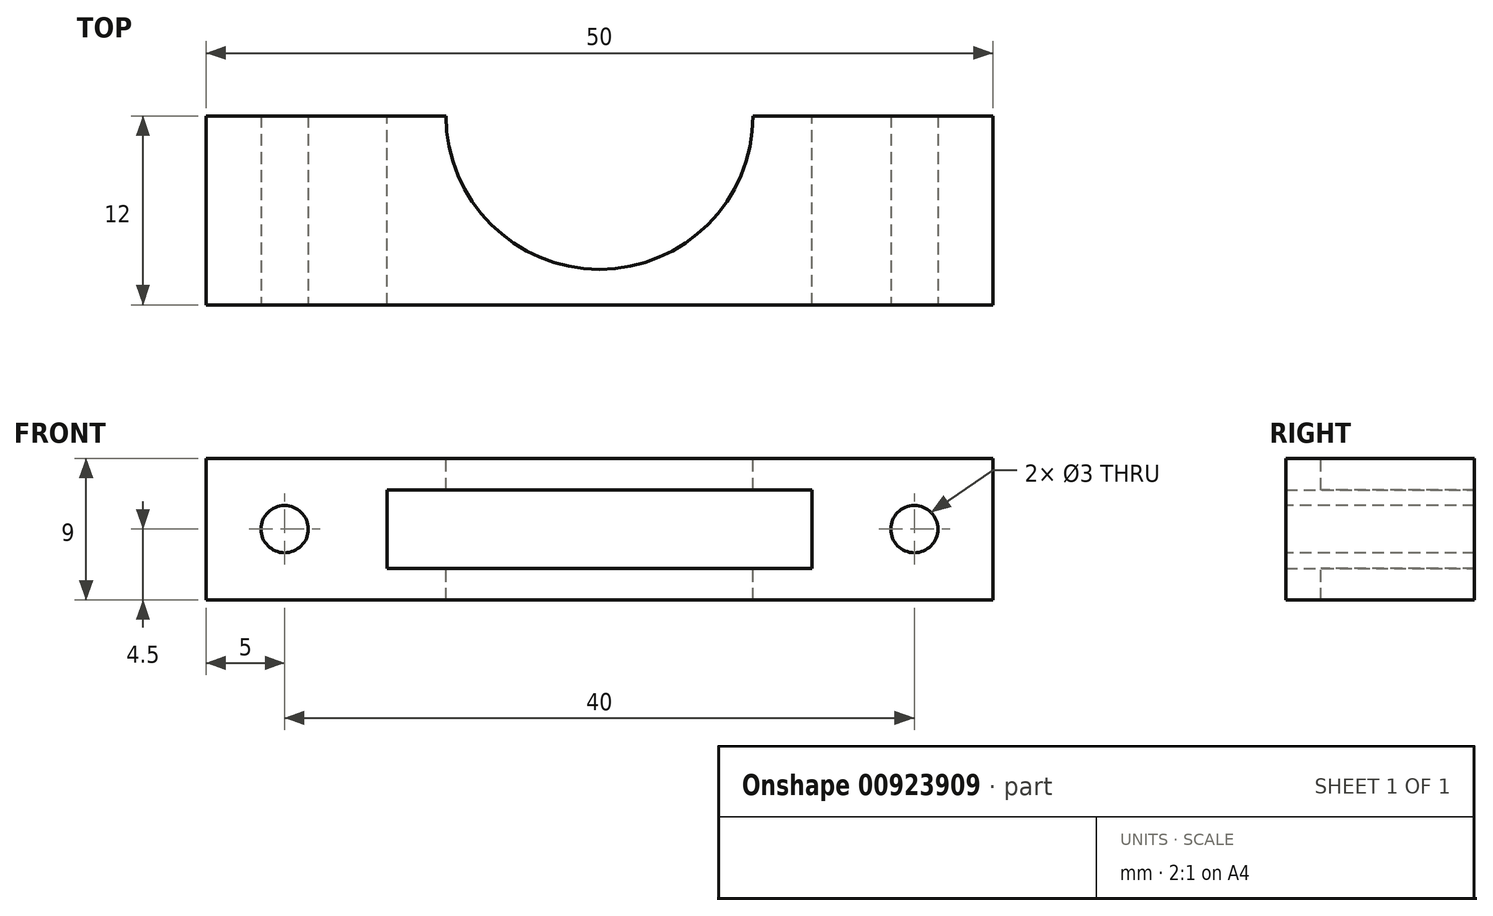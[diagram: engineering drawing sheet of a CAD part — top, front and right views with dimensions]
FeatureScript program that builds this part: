
annotation { "Feature Type Name" : "Feature", "Feature Type Description" : "" }
export const myFeature = defineFeature(function(context is Context, id is Id, definition is map)
    precondition{}
    {
        {
            var Q0;
            Q0=qCreatedBy(makeId("Top.planeOp"),FACE);
            var sketch = newSketch(context, id + "F0", { "sketchPlane" : qUnion([Q0])});
            skLineSegment(sketch, "E0.bottom", {"start": v(0, 0) * mm, "end": v(50, 0) * mm});
            skLineSegment(sketch, "E0.top", {"start": v(0, 12) * mm, "end": v(50, 12) * mm});
            skLineSegment(sketch, "E0.left", {"start": v(0, 0) * mm, "end": v(0, 12) * mm});
            skLineSegment(sketch, "E0.right", {"start": v(50, 0) * mm, "end": v(50, 12) * mm});
            skSolve(sketch);
        }
        {
            var Q0;
            Q0=makeQuery(id+"F0.imprint","IMPRINT",FACE,{"disambiguationData":[TD([[makeQuery(id+"F0.imprint","IMPRINT",EDGE,{"derivedFrom":sQuery(id+"F0.wireOp",EDGE,"E0.bottom")}),1.0]])]});
            extrude(context, id + "F1", {"entities" : qUnion([Q0]), "depth" : 9 * mm, "offsetDistance" : 25 * mm});
        }
        {
            var Q0;
            Q0=makeQuery(id+"F1.opExtrude","SWEPT_FACE",FACE,{"disambiguationData":[OSD([sQuery(id+"F0.wireOp",EDGE,"E0.bottom")])]});
            var sketch = newSketch(context, id + "F2", { "sketchPlane" : qUnion([Q0])});
            skCircle(sketch, "E1", {"center": v(5, 4.5) * mm, "radius": 1.5 * mm});
            skCircle(sketch, "E2", {"center": v(45, 4.5) * mm, "radius": 1.5 * mm});
            skSolve(sketch);
        }
        {
            var Q0;
            Q0=makeQuery(id+"F2.imprint","IMPRINT",FACE,{"disambiguationData":[TD([[makeQuery(id+"F2.imprint","IMPRINT",EDGE,{"derivedFrom":sQuery(id+"F2.wireOp",EDGE,"E1")}),1.0]])]});
            var Q1;
            Q1=makeQuery(id+"F2.imprint","IMPRINT",FACE,{"disambiguationData":[TD([[makeQuery(id+"F2.imprint","IMPRINT",EDGE,{"derivedFrom":sQuery(id+"F2.wireOp",EDGE,"E2")}),1.0]])]});
            extrude(context, id + "F3", {"entities" : qUnion([Q0, Q1]), "operationType" : NewBodyOperationType.REMOVE, "oppositeDirection" : true, "depth" : 12 * mm, "offsetDistance" : 25 * mm});
        }
        {
            var Q0;
            Q0=makeQuery(id+"F1.opExtrude","SWEPT_FACE",FACE,{"disambiguationData":[OSD([sQuery(id+"F0.wireOp",EDGE,"E0.top")])]});
            var sketch = newSketch(context, id + "F4", { "sketchPlane" : qUnion([Q0])});
            skLineSegment(sketch, "E3.bottom", {"start": v(-38.5, 2) * mm, "end": v(-11.5, 2) * mm});
            skLineSegment(sketch, "E3.top", {"start": v(-38.5, 7) * mm, "end": v(-11.5, 7) * mm});
            skLineSegment(sketch, "E3.left", {"start": v(-38.5, 2) * mm, "end": v(-38.5, 7) * mm});
            skLineSegment(sketch, "E3.right", {"start": v(-11.5, 2) * mm, "end": v(-11.5, 7) * mm});
            skSolve(sketch);
        }
        {
            var Q0;
            Q0=makeQuery(id+"F4.imprint","IMPRINT",FACE,{"disambiguationData":[TD([[makeQuery(id+"F4.imprint","IMPRINT",EDGE,{"derivedFrom":sQuery(id+"F4.wireOp",EDGE,"E3.bottom")}),1.0]])]});
            extrude(context, id + "F5", {"entities" : qUnion([Q0]), "operationType" : NewBodyOperationType.REMOVE, "oppositeDirection" : true, "depth" : 12.5 * mm, "offsetDistance" : 25 * mm});
        }
        {
            var Q0;
            Q0=makeQuery(id+"F1.opExtrude","CAP_FACE",FACE,{"disambiguationData":[OSD([sQuery(id+"F0.wireOp",EDGE,"E0.bottom"),sQuery(id+"F0.wireOp",EDGE,"E0.top"),sQuery(id+"F0.wireOp",EDGE,"E0.left"),sQuery(id+"F0.wireOp",EDGE,"E0.right")])],"isStart":false});
            var sketch = newSketch(context, id + "F6", { "sketchPlane" : qUnion([Q0])});
            skCircle(sketch, "E4", {"center": v(25, 12) * mm, "radius": 9.75 * mm});
            skSolve(sketch);
        }
        {
            var Q0;
            {var subQ0=sQuery(id+"F6.wireOp",EDGE,"E4");var subQ1=makeQuery(id+"F1.opExtrude","CAP_EDGE",EDGE,{"disambiguationData":[OSD([sQuery(id+"F0.wireOp",EDGE,"E0.top")])],"isStart":false});var subQ2=makeQuery(id+"F6.imprint","INTERSECT",VERTEX,{"disambiguationData":[OD(0.0)],"derivedFrom":[subQ1,subQ0]});Q0=makeQuery(id+"F6.imprint","IMPRINT",FACE,{"disambiguationData":[TD([[makeQuery(id+"F6.imprint","IMPRINT",EDGE,{"disambiguationData":[TD([[subQ2,-1.0]])],"derivedFrom":subQ0}),1.0]])]});}
            extrude(context, id + "F7", {"entities" : qUnion([Q0]), "operationType" : NewBodyOperationType.REMOVE, "oppositeDirection" : true, "depth" : 9 * mm, "offsetDistance" : 25 * mm});
        }
    });
